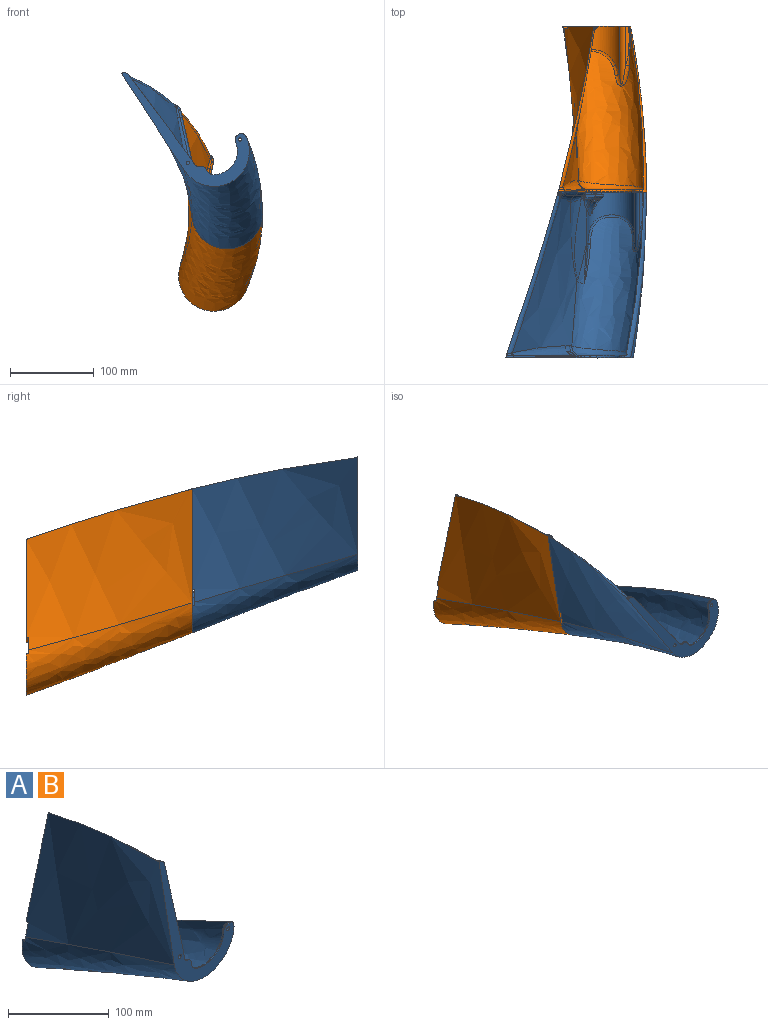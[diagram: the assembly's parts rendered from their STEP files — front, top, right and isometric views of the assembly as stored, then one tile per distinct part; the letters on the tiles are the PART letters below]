
ASSEMBLY  parts=2 mates=1
PART A: 119 faces, bbox 147.3x214.7x331.7 mm
  f0: cylinder r=28mm len=1.14mm, axis (0,-1,0), area 1mm2, adj f9,f12,f92,f104
  f1: cylinder r=1.9mm len=5mm, axis (0,1,0), area 59.7mm2, adj f23,f86
  f2: bspline ~23.71x23.52mm, area 218.3mm2, adj f3,f5,f74,f78,f79,f87
  f3: bspline ~16.28x15.4mm, area 108.8mm2, adj f2,f6,f74,f76,f81,f87
  f4: bspline ~198x173.4mm, area 25594.1mm2, adj f9,f13,f16,f19,f22,f23
  f5: cylinder r=28mm len=60.32mm, axis (0,1,0), area 2510.6mm2, adj f2,f6,f15,f19,f32,f33,f77,f78
  f6: cylinder r=15mm len=40.23mm, axis (0,1,0), area 217.3mm2, adj f3,f5,f25,f28,f34
  f7: bspline ~198.89x65.99mm, area 1411.7mm2, adj f16,f17,f42,f43,f44,f69,f70
  f8: plane 65.45x38.93mm, normal (0,1,0), area 448.7mm2, adj f47,f54,f94,f95,f96,f97,f98,f99
  f9: plane 172.05x105.71mm, normal (0,-1,0), area 3034.5mm2, adj f0,f4,f10,f12,f13,f16,f18,f24
  f10: cylinder r=2mm len=4mm, axis (0,-1,0), area 37.7mm2, adj f9,f48
  f11: bspline ~11.51x11.49mm, area 110.8mm2, adj f17,f45,f46,f49,f106
  f12: plane 10.77x1.71mm, normal (0.99,0,0.16), area 12.6mm2, adj f0,f9,f40,f105,f106
  f13: bspline ~211.61x111.35mm, area 1755mm2, adj f4,f9,f14,f19,f50,f51,f93,f94
  f14: bspline ~198x166.36mm, area 17467.1mm2, adj f13,f17,f26,f30,f31,f32,f33,f34
  f15: cylinder r=6mm len=69.1mm, axis (0,1,0), area 557.7mm2, adj f5,f19,f29,f31
  f16: bspline ~201.98x195.33mm, area 27429.8mm2, adj f4,f7,f9,f20,f21,f23,f41,f42
  f17: bspline ~327.28x198mm, area 20505.5mm2, adj f7,f11,f14,f27,f45,f46,f57,f58
  f18: cylinder r=28mm len=37.65mm, axis (0,-1,0), area 44.2mm2, adj f9,f24,f90,f98
  f19: plane 81.33x49.79mm, normal (0,1,0), area 1525.8mm2, adj f4,f5,f13,f15,f22,f29,f36,f50
  f20: plane 123.75x37.11mm, normal (0,1,0), area 1215.6mm2, adj f16,f21,f55,f61,f62,f63,f64,f65
  f21: plane 12.99x5.86mm, normal (-0.41,0,-0.91), area 41.4mm2, adj f16,f20,f23,f61
  f22: plane 15.95x7.13mm, normal (0.41,0,0.91), area 51.9mm2, adj f4,f19,f23,f89
  f23: plane 35.05x32.73mm, normal (0,1,0), area 610.1mm2, adj f1,f4,f16,f21,f22,f37,f72,f73
  f24: cylinder r=30mm len=1mm, axis (0,-1,0), area 0.6mm2, adj f9,f18,f53,f97
  f25: plane 101.04x35.78mm, normal (1,0,0.05), area 2061.4mm2, adj f6,f26,f27,f60,f75,f76,f85
  f26: bspline ~56.49x52.93mm, area 335.2mm2, adj f14,f25,f27,f28
  f27: bspline ~111.52x43.97mm, area 1487.9mm2, adj f17,f25,f26,f59
  f28: bspline ~50.49x17.06mm, area 189.5mm2, adj f6,f26,f35
  f29: plane 47.5x4.64mm, normal (0.34,0,0.94), area 164.5mm2, adj f15,f19,f30,f50
  f30: bspline ~14.69x4.92mm, area 46.7mm2, adj f14,f29,f31,f50
  f31: bspline ~24.49x17mm, area 198.3mm2, adj f14,f15,f30,f32
  f32: bspline ~13.3x8.67mm, area 72.6mm2, adj f5,f14,f31,f33
  f33: bspline ~51.27x41.7mm, area 332.3mm2, adj f5,f14,f32,f34
  f34: bspline ~7.4x7.15mm, area 7mm2, adj f6,f14,f33,f35
  f35: bspline ~49.56x23.02mm, area 164.3mm2, adj f14,f28,f34
  f36: cylinder r=1.9mm len=30mm, axis (0,1,0), area 358.1mm2, adj f19,f39
  f37: cylinder r=1.9mm len=27mm, axis (0,1,0), area 322.3mm2, adj f23,f38
  f38: cone r=1.9mm half-angle=20.8deg, axis (0,1,0), area 31.9mm2, adj f37
  f39: cone r=1.9mm half-angle=20.8deg, axis (0,1,0), area 31.9mm2, adj f36
  f40: plane 117.44x26.27mm, normal (0.98,0,0.22), area 234.8mm2, adj f9,f12,f41,f107,f108,f109
  f41: bspline ~10.58x8.59mm, area 31.1mm2, adj f9,f16,f40,f110,f111,f112
  f42: bspline ~7.64x6.87mm, area 20.3mm2, adj f7,f16,f43,f111,f112
  f43: bspline ~3.02x2.41mm, area 3.5mm2, adj f7,f42,f44,f109,f110
  f44: bspline ~3.19x3.1mm, area 3.7mm2, adj f7,f43,f45,f108
  f45: bspline ~117.24x28.86mm, area 1286.1mm2, adj f11,f17,f44,f107
  f46: bspline ~11.83x11.39mm, area 87.6mm2, adj f11,f17,f47,f103,f104,f105
  f47: bspline ~78.25x49.42mm, area 1130.6mm2, adj f8,f14,f46,f93,f102
  f48: plane 8x8mm, normal (0,1,0), area 37.7mm2, adj f10,f49
  f49: cylinder r=4mm len=8mm, axis (0,-1,0), area 49.5mm2, adj f11,f48,f106
  f50: bspline ~43.27x3.19mm, area 61mm2, adj f13,f14,f19,f29,f30
  f51: plane 4.95x1.01mm, normal (-0.07,0,1), area 4.6mm2, adj f9,f13,f52,f94
  f52: cylinder r=6mm len=5.98mm, axis (0,-1,0), area 9mm2, adj f9,f51,f53,f95
  f53: cylinder r=28mm len=11.78mm, axis (0,-1,0), area 12.2mm2, adj f9,f24,f52,f96
  f54: cylinder r=2mm len=4mm, axis (0,-1,0), area 37.7mm2, adj f8,f9
  f55: extruded ~1.91x1.18mm, area 0.5mm2, adj f20,f67,f68,f70
  f56: bspline ~4.35x3.53mm, area 0mm2, adj f57,f68
  f57: bspline ~45.35x15.74mm, area 52mm2, adj f17,f56,f58,f64,f66,f67
  f58: bspline ~61.55x19.11mm, area 505.4mm2, adj f17,f57,f59,f63
  f59: bspline ~39.11x9.03mm, area 329.9mm2, adj f27,f58,f60,f62
  f60: bspline ~6.98x4.28mm, area 24mm2, adj f25,f59,f61,f85,f115
  f61: bspline ~9.62x4.06mm, area 32.4mm2, adj f20,f21,f60,f62,f114
  f62: bspline ~38.32x9.83mm, area 192.5mm2, adj f20,f59,f61,f63
  f63: bspline ~61.34x15.31mm, area 307.5mm2, adj f20,f58,f62,f64
  f64: bspline ~9.89x4.47mm, area 41.6mm2, adj f20,f57,f63,f65
  f65: bspline ~3.52x2.55mm, area 0.3mm2, adj f20,f64,f66
  f66: bspline ~6.88x3.87mm, area 24.4mm2, adj f20,f57,f65,f67
  f67: bspline ~5.58x4.35mm, area 4.5mm2, adj f55,f57,f66,f68
  f68: bspline ~6.47x6.24mm, area 10mm2, adj f55,f56,f67,f69
  f69: bspline ~6.06x4.98mm, area 10mm2, adj f7,f68,f70
  f70: bspline ~0.63x0.48mm, area 0.3mm2, adj f7,f20,f55,f69
  f71: plane 4.06x0.8mm, normal (0.41,0,0.91), area 2.2mm2, adj f73,f114,f115
  f72: cylinder r=10mm len=19.01mm, axis (0,1,0), area 68mm2, adj f23,f73,f77,f79,f80,f81,f82
  f73: plane 11.99x5.91mm, normal (0.41,0,0.91), area 37.6mm2, adj f23,f71,f72,f83,f84
  f74: plane 10.03x2.82mm, normal (0,-1,0), area 9.2mm2, adj f2,f3,f80
  f75: bspline ~10.63x8.25mm, area 43.4mm2, adj f25,f76,f84,f85
  f76: bspline ~13.35x13.2mm, area 56mm2, adj f3,f25,f75,f82,f83
  f77: bspline ~25.03x20.76mm, area 253.9mm2, adj f5,f23,f72,f78,f88
  f78: bspline ~18.62x12.23mm, area 53.1mm2, adj f2,f5,f77,f79
  f79: bspline ~6.83x5.78mm, area 25.2mm2, adj f2,f72,f78,f80
  f80: cone r=10mm half-angle=45deg, axis (0,1,0), area 41.5mm2, adj f72,f74,f79,f81
  f81: bspline ~3.93x3.86mm, area 11.3mm2, adj f3,f72,f80,f82
  f82: bspline ~2.49x2.21mm, area 0.2mm2, adj f72,f76,f81,f83
  f83: bspline ~4.5x3.98mm, area 13.5mm2, adj f73,f76,f82,f84
  f84: bspline ~7.33x4.63mm, area 17.7mm2, adj f73,f75,f83,f85
  f85: bspline ~8.94x5.99mm, area 6.4mm2, adj f25,f60,f75,f84,f115
  f86: plane 8x8mm, normal (0,-1,0), area 38.9mm2, adj f1,f87
  f87: cylinder r=4mm len=8mm, axis (0,1,0), area 56.6mm2, adj f2,f3,f86
  f88: extruded ~14.2x3.5mm, area 41.2mm2, adj f5,f19,f77,f113
  f89: cylinder r=6mm len=8.05mm, axis (0,-1,0), area 14.3mm2, adj f19,f22,f113
  f90: cylinder r=10mm len=8.91mm, axis (0,-1,0), area 10.7mm2, adj f9,f18,f91,f99
  f91: cylinder r=6mm len=6.07mm, axis (0,-1,0), area 8.6mm2, adj f9,f90,f92,f100
  f92: cylinder r=6mm len=4.93mm, axis (0,-1,0), area 7.6mm2, adj f0,f9,f91,f101,f102,f103
  f93: bspline ~2.86x2.84mm, area 0.7mm2, adj f13,f14,f47,f94
  f94: cylinder r=2mm len=4.56mm, axis (-1,0,-0.07), area 13.8mm2, adj f8,f13,f51,f93,f95
  f95: torus R=4mm, axis (0,-1,0), area 24.8mm2, adj f8,f52,f94,f96
  f96: torus R=30mm, axis (0,-1,0), area 39.3mm2, adj f8,f53,f95,f97
  f97: torus R=28mm, axis (0,-1,0), area 1.9mm2, adj f8,f24,f96,f98
  f98: torus R=30mm, axis (0,-1,0), area 142.4mm2, adj f8,f18,f97,f99
  f99: torus R=12mm, axis (0,-1,0), area 36.2mm2, adj f8,f90,f98,f100
  f100: torus R=4mm, axis (0,-1,0), area 23.7mm2, adj f8,f91,f99,f101
  f101: torus R=8mm, axis (0,-1,0), area 12.1mm2, adj f8,f92,f100,f102
  f102: bspline ~2.89x2.7mm, area 3.5mm2, adj f47,f92,f101,f103
  f103: bspline ~5.51x3.22mm, area 9.3mm2, adj f46,f92,f102,f104
  f104: bspline ~4.97x2.5mm, area 2.7mm2, adj f0,f46,f103,f105
  f105: bspline ~3.48x2.2mm, area 1.9mm2, adj f12,f46,f104,f106
  f106: bspline ~10.46x3.27mm, area 29.2mm2, adj f11,f12,f49,f105,f107
  f107: bspline ~116.15x26.1mm, area 202.5mm2, adj f40,f45,f106,f108
  f108: bspline ~0.95x0.4mm, area 0.3mm2, adj f40,f44,f107,f109
  f109: bspline ~0.23x0.21mm, area 0mm2, adj f40,f43,f108,f110
  f110: bspline ~0.96x0.45mm, area 0.3mm2, adj f41,f43,f109,f111
  f111: bspline ~1.77x1.02mm, area 0.5mm2, adj f41,f42,f110,f112
  f112: bspline ~5.38x2.9mm, area 0.7mm2, adj f41,f42,f111
  f113: bspline ~10.07x6.05mm, area 12.7mm2, adj f23,f88,f89
  f114: bspline ~1.31x0.87mm, area 0.3mm2, adj f61,f71,f115
  f115: bspline ~3.07x2.95mm, area 3.3mm2, adj f60,f71,f85,f114
  f116: bspline ~103.4x100.46mm, area 0mm2, adj f117,f118
  f117: plane 23.48x0.86mm, normal (0.26,0,0.97), area 4.7mm2, adj f116,f118
  f118: plane 23.3x0.72mm, normal (0,0,-1), area 5mm2, adj f116,f117
PART B: same geometry as A
PLACE A rot(axis=(0,-1,0),24deg) t=(90.48,-86.48,104.61)mm
PLACE B t=(90.48,111.52,104.47)mm fixed
MATE revolute B.f49 <-> A.f37  axis (0,-1,0) through (239.28,111.52,104.47)mm
